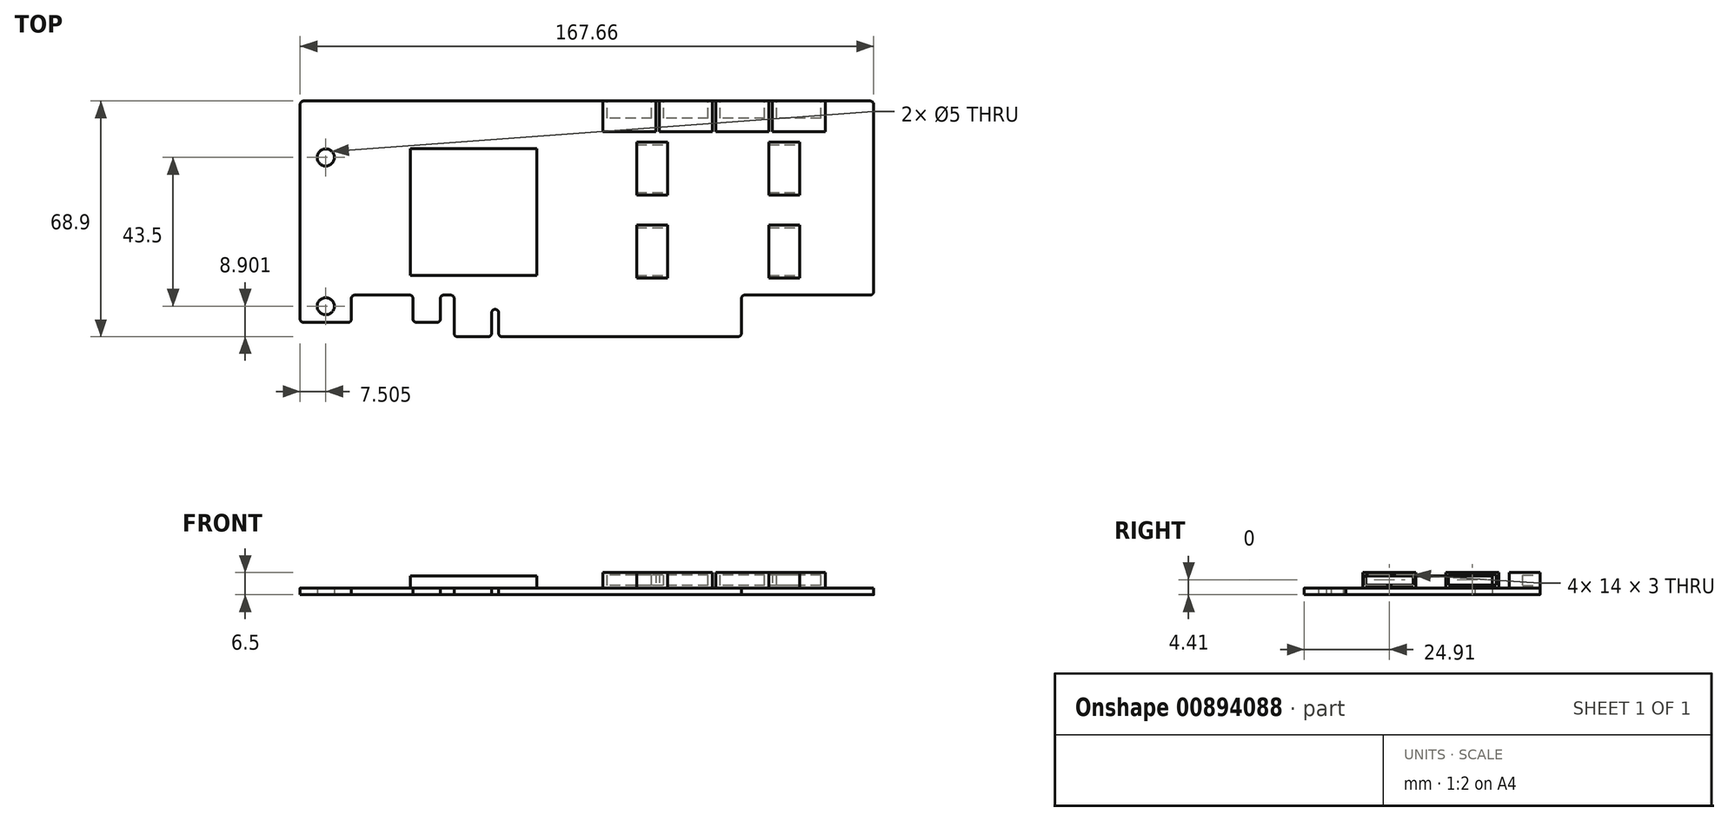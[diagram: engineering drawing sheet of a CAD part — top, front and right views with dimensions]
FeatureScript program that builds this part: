
annotation { "Feature Type Name" : "Feature", "Feature Type Description" : "" }
export const myFeature = defineFeature(function(context is Context, id is Id, definition is map)
    precondition{}
    {
        {
            var Q0;
            Q0=qCreatedBy(makeId("Top.planeOp"),FACE);
            var sketch = newSketch(context, id + "F0", { "sketchPlane" : qUnion([Q0])});
            skLineSegment(sketch, "E0.top", {"start": v(83.83, 32.37) * mm, "end": v(-83.83, 32.37) * mm});
            skLineSegment(sketch, "E0.right", {"start": v(-83.83, -32.37) * mm, "end": v(-83.83, 32.37) * mm});
            skPoint(sketch, "E0.middle", {"position": v(0, 0) * mm});
            skLineSegment(sketch, "E1", {"start": v(-83.83, -32.37) * mm, "end": v(-68.83, -32.37) * mm});
            skLineSegment(sketch, "E2", {"start": v(-68.83, -32.37) * mm, "end": v(-68.83, -24.37) * mm});
            skLineSegment(sketch, "E3", {"start": v(-68.83, -24.37) * mm, "end": v(-50.82, -24.37) * mm});
            skLineSegment(sketch, "E4", {"start": v(-50.82, -24.37) * mm, "end": v(-50.82, -32.37) * mm});
            skLineSegment(sketch, "E5", {"start": v(-50.82, -32.37) * mm, "end": v(-42.83, -32.37) * mm});
            skLineSegment(sketch, "E6", {"start": v(-42.83, -32.37) * mm, "end": v(-42.82, -24.37) * mm});
            skLineSegment(sketch, "E7", {"start": v(-42.82, -24.37) * mm, "end": v(-38.82, -24.37) * mm});
            skLineSegment(sketch, "E8", {"start": v(-38.82, -24.37) * mm, "end": v(-38.82, -36.53) * mm});
            skLineSegment(sketch, "E9", {"start": v(-38.82, -36.53) * mm, "end": v(-27.82, -36.53) * mm});
            skLineSegment(sketch, "E10", {"start": v(-27.82, -36.53) * mm, "end": v(-27.82, -28.53) * mm});
            skLineSegment(sketch, "E11", {"start": v(-27.82, -28.53) * mm, "end": v(-25.82, -28.53) * mm});
            skLineSegment(sketch, "E12", {"start": v(-25.82, -28.53) * mm, "end": v(-25.82, -36.53) * mm});
            skLineSegment(sketch, "E13", {"start": v(-25.82, -36.53) * mm, "end": v(45.18, -36.53) * mm});
            skLineSegment(sketch, "E14", {"start": v(45.18, -36.53) * mm, "end": v(45.18, -24.37) * mm});
            skLineSegment(sketch, "E15", {"start": v(83.83, 32.37) * mm, "end": v(83.83, -24.37) * mm});
            skCircle(sketch, "E16", {"center": v(-76.33, -27.63) * mm, "radius": 2.5 * mm});
            skCircle(sketch, "E17.MirrorC", {"center": v(-76.33, 15.87) * mm, "radius": 2.5 * mm});
            skLineSegment(sketch, "E18", {"start": v(45.18, -24.37) * mm, "end": v(83.82, -24.37) * mm});
            skLineSegment(sketch, "E19", {"start": v(-76.33, 15.87) * mm, "end": v(-76.33, -27.63) * mm, "construction": true});
            skLineSegment(sketch, "E20", {"start": v(-76.33, 15.87) * mm, "end": v(-76.33, 32.37) * mm, "construction": true});
            skLineSegment(sketch, "E21", {"start": v(-83.83, 0) * mm, "end": v(-76.33, 0) * mm, "construction": true});
            skSolve(sketch);
        }
        {
            var Q0;
            Q0=qSketchRegion(id+"F0",true);
            extrude(context, id + "F1", {"entities" : qUnion([Q0]), "depth" : 2 * mm});
        }
        {
            var Q0;
            Q0=makeQuery(id+"F1.opExtrude","CAP_FACE",FACE,{"disambiguationData":[OSD([sQuery(id+"F0.wireOp",EDGE,"E0.top"),sQuery(id+"F0.wireOp",EDGE,"E0.right"),sQuery(id+"F0.wireOp",EDGE,"E1"),sQuery(id+"F0.wireOp",EDGE,"E2"),sQuery(id+"F0.wireOp",EDGE,"E3"),sQuery(id+"F0.wireOp",EDGE,"E4"),sQuery(id+"F0.wireOp",EDGE,"E5"),sQuery(id+"F0.wireOp",EDGE,"E6"),sQuery(id+"F0.wireOp",EDGE,"E7"),sQuery(id+"F0.wireOp",EDGE,"E8"),sQuery(id+"F0.wireOp",EDGE,"E9"),sQuery(id+"F0.wireOp",EDGE,"E10"),sQuery(id+"F0.wireOp",EDGE,"E11"),sQuery(id+"F0.wireOp",EDGE,"E12"),sQuery(id+"F0.wireOp",EDGE,"E13"),sQuery(id+"F0.wireOp",EDGE,"E14"),sQuery(id+"F0.wireOp",EDGE,"E15"),sQuery(id+"F0.wireOp",EDGE,"E16"),sQuery(id+"F0.wireOp",EDGE,"E17.MirrorC"),sQuery(id+"F0.wireOp",EDGE,"E18")])],"isStart":false});
            var sketch = newSketch(context, id + "F2", { "sketchPlane" : qUnion([Q0])});
            skLineSegment(sketch, "E22.bottom", {"start": v(-77.83, 23.37) * mm, "end": v(-62.33, 23.37) * mm});
            skLineSegment(sketch, "E22.top", {"start": v(-77.83, 32.37) * mm, "end": v(-62.33, 32.37) * mm});
            skLineSegment(sketch, "E22.left", {"start": v(-77.83, 23.37) * mm, "end": v(-77.83, 32.37) * mm});
            skLineSegment(sketch, "E22.right", {"start": v(-62.33, 23.37) * mm, "end": v(-62.33, 32.37) * mm});
            skLineSegment(sketch, "E23", {"start": v(-77.83, 32.37) * mm, "end": v(-83.83, 32.37) * mm, "construction": true});
            skLineSegment(sketch, "E24.1.0.0", {"start": v(-61.33, 32.37) * mm, "end": v(-45.83, 32.37) * mm});
            skLineSegment(sketch, "E24.1.0.1", {"start": v(-61.33, 23.37) * mm, "end": v(-61.33, 32.37) * mm});
            skLineSegment(sketch, "E24.1.0.2", {"start": v(-61.33, 23.37) * mm, "end": v(-45.83, 23.37) * mm});
            skLineSegment(sketch, "E24.1.0.3", {"start": v(-45.83, 23.37) * mm, "end": v(-45.83, 32.37) * mm});
            skLineSegment(sketch, "E24.2.0.0", {"start": v(-44.83, 32.37) * mm, "end": v(-29.33, 32.37) * mm});
            skLineSegment(sketch, "E24.2.0.1", {"start": v(-44.83, 23.37) * mm, "end": v(-44.83, 32.37) * mm});
            skLineSegment(sketch, "E24.2.0.2", {"start": v(-44.83, 23.37) * mm, "end": v(-29.33, 23.37) * mm});
            skLineSegment(sketch, "E24.2.0.3", {"start": v(-29.33, 23.37) * mm, "end": v(-29.33, 32.37) * mm});
            skLineSegment(sketch, "E24.direction1", {"start": v(-77.83, 32.37) * mm, "end": v(-61.33, 32.37) * mm, "construction": true});
            skLineSegment(sketch, "E25.0.3.0", {"start": v(-28.33, 32.37) * mm, "end": v(-12.83, 32.37) * mm});
            skLineSegment(sketch, "E25.3.3.0", {"start": v(-28.33, 23.37) * mm, "end": v(-28.33, 32.37) * mm});
            skLineSegment(sketch, "E25.6.3.0", {"start": v(-28.33, 23.37) * mm, "end": v(-12.83, 23.37) * mm});
            skLineSegment(sketch, "E25.9.3.0", {"start": v(-12.83, 23.37) * mm, "end": v(-12.83, 32.37) * mm});
            skLineSegment(sketch, "E25.0.4.0", {"start": v(-11.83, 32.37) * mm, "end": v(3.67, 32.37) * mm});
            skLineSegment(sketch, "E25.3.4.0", {"start": v(-11.83, 23.37) * mm, "end": v(-11.83, 32.37) * mm});
            skLineSegment(sketch, "E25.6.4.0", {"start": v(-11.83, 23.37) * mm, "end": v(3.67, 23.37) * mm});
            skLineSegment(sketch, "E25.9.4.0", {"start": v(3.67, 23.37) * mm, "end": v(3.67, 32.37) * mm});
            skLineSegment(sketch, "E25.0.5.0", {"start": v(4.67, 32.37) * mm, "end": v(20.17, 32.37) * mm});
            skLineSegment(sketch, "E25.3.5.0", {"start": v(4.67, 23.37) * mm, "end": v(4.67, 32.37) * mm});
            skLineSegment(sketch, "E25.6.5.0", {"start": v(4.67, 23.37) * mm, "end": v(20.17, 23.37) * mm});
            skLineSegment(sketch, "E25.9.5.0", {"start": v(20.17, 23.37) * mm, "end": v(20.17, 32.37) * mm});
            skLineSegment(sketch, "E25.0.6.0", {"start": v(21.17, 32.37) * mm, "end": v(36.67, 32.37) * mm});
            skLineSegment(sketch, "E25.3.6.0", {"start": v(21.17, 23.37) * mm, "end": v(21.17, 32.37) * mm});
            skLineSegment(sketch, "E25.6.6.0", {"start": v(21.17, 23.37) * mm, "end": v(36.67, 23.37) * mm});
            skLineSegment(sketch, "E25.9.6.0", {"start": v(36.67, 23.37) * mm, "end": v(36.67, 32.37) * mm});
            skLineSegment(sketch, "E25.0.7.0", {"start": v(37.67, 32.37) * mm, "end": v(53.17, 32.37) * mm});
            skLineSegment(sketch, "E25.3.7.0", {"start": v(37.67, 23.37) * mm, "end": v(37.67, 32.37) * mm});
            skLineSegment(sketch, "E25.6.7.0", {"start": v(37.67, 23.37) * mm, "end": v(53.17, 23.37) * mm});
            skLineSegment(sketch, "E25.9.7.0", {"start": v(53.17, 23.37) * mm, "end": v(53.17, 32.37) * mm});
            skLineSegment(sketch, "E25.0.8.0", {"start": v(54.17, 32.37) * mm, "end": v(69.67, 32.37) * mm});
            skLineSegment(sketch, "E25.3.8.0", {"start": v(54.17, 23.37) * mm, "end": v(54.17, 32.37) * mm});
            skLineSegment(sketch, "E25.6.8.0", {"start": v(54.17, 23.37) * mm, "end": v(69.67, 23.37) * mm});
            skLineSegment(sketch, "E25.9.8.0", {"start": v(69.67, 23.37) * mm, "end": v(69.67, 32.37) * mm});
            skLineSegment(sketch, "E26", {"start": v(53.17, 23.37) * mm, "end": v(53.17, 20.37) * mm, "construction": true});
            skLineSegment(sketch, "E27.bottom", {"start": v(53.17, 20.37) * mm, "end": v(62.17, 20.37) * mm});
            skLineSegment(sketch, "E27.top", {"start": v(53.17, 4.87) * mm, "end": v(62.17, 4.87) * mm});
            skLineSegment(sketch, "E27.left", {"start": v(53.17, 20.37) * mm, "end": v(53.17, 4.87) * mm});
            skLineSegment(sketch, "E27.right", {"start": v(62.17, 20.37) * mm, "end": v(62.17, 4.87) * mm});
            skLineSegment(sketch, "E28.bottom", {"start": v(53.17, -19.37) * mm, "end": v(62.17, -19.37) * mm});
            skLineSegment(sketch, "E28.top", {"start": v(53.17, -3.87) * mm, "end": v(62.17, -3.87) * mm});
            skLineSegment(sketch, "E28.left", {"start": v(53.17, -19.37) * mm, "end": v(53.17, -3.87) * mm});
            skLineSegment(sketch, "E28.right", {"start": v(62.17, -19.37) * mm, "end": v(62.17, -3.87) * mm});
            skLineSegment(sketch, "E29", {"start": v(53.17, 4.87) * mm, "end": v(53.17, -3.87) * mm, "construction": true});
            skLineSegment(sketch, "E30", {"start": v(53.17, -19.37) * mm, "end": v(53.17, -24.37) * mm, "construction": true});
            skLineSegment(sketch, "E31", {"start": v(53.17, 0.5) * mm, "end": v(23.53, 0.5) * mm, "construction": true});
            skLineSegment(sketch, "E32", {"start": v(38.35, 5.58) * mm, "end": v(38.35, -5.04) * mm, "construction": true});
            skPoint(sketch, "E32.startSnap0", {"position": v(38.35, 0.5) * mm});
            skLineSegment(sketch, "E33.MirrorCS", {"start": v(23.53, 20.37) * mm, "end": v(23.53, 4.87) * mm});
            skLineSegment(sketch, "E34.MirrorCS", {"start": v(23.53, 20.37) * mm, "end": v(14.53, 20.37) * mm});
            skLineSegment(sketch, "E35.MirrorCS", {"start": v(14.53, 20.37) * mm, "end": v(14.53, 4.87) * mm});
            skLineSegment(sketch, "E36.MirrorCS", {"start": v(23.53, 4.87) * mm, "end": v(14.53, 4.87) * mm});
            skLineSegment(sketch, "E37.MirrorCS", {"start": v(23.53, -3.87) * mm, "end": v(14.53, -3.87) * mm});
            skLineSegment(sketch, "E38.MirrorCS", {"start": v(23.53, -19.37) * mm, "end": v(23.53, -3.87) * mm});
            skLineSegment(sketch, "E39.MirrorCS", {"start": v(23.53, -19.37) * mm, "end": v(14.53, -19.37) * mm});
            skLineSegment(sketch, "E40.MirrorCS", {"start": v(14.53, -19.37) * mm, "end": v(14.53, -3.87) * mm});
            skLineSegment(sketch, "E41.bottom", {"start": v(-51.64, -18.59) * mm, "end": v(-14.64, -18.59) * mm});
            skLineSegment(sketch, "E41.top", {"start": v(-51.64, 18.41) * mm, "end": v(-14.64, 18.41) * mm});
            skLineSegment(sketch, "E41.left", {"start": v(-51.64, -18.59) * mm, "end": v(-51.64, 18.41) * mm});
            skLineSegment(sketch, "E41.right", {"start": v(-14.64, -18.59) * mm, "end": v(-14.64, 18.41) * mm});
            skSolve(sketch);
        }
        {
            var Q0;
            Q0=makeQuery(id+"F1.opExtrude","SWEPT_EDGE",EDGE,{"disambiguationData":[OSD([sQuery(id+"F0.wireOp",EDGE,"E0.right"),sQuery(id+"F0.wireOp",EDGE,"E1")])]});
            var Q1;
            Q1=makeQuery(id+"F1.opExtrude","SWEPT_EDGE",EDGE,{"disambiguationData":[OSD([sQuery(id+"F0.wireOp",EDGE,"E1"),sQuery(id+"F0.wireOp",EDGE,"E2")])]});
            var Q2;
            Q2=makeQuery(id+"F1.opExtrude","SWEPT_EDGE",EDGE,{"disambiguationData":[OSD([sQuery(id+"F0.wireOp",EDGE,"E2"),sQuery(id+"F0.wireOp",EDGE,"E3")])]});
            var Q3;
            Q3=makeQuery(id+"F1.opExtrude","SWEPT_EDGE",EDGE,{"disambiguationData":[OSD([sQuery(id+"F0.wireOp",EDGE,"E4"),sQuery(id+"F0.wireOp",EDGE,"E5")])]});
            var Q4;
            Q4=makeQuery(id+"F1.opExtrude","SWEPT_EDGE",EDGE,{"disambiguationData":[OSD([sQuery(id+"F0.wireOp",EDGE,"E5"),sQuery(id+"F0.wireOp",EDGE,"E6")])]});
            var Q5;
            Q5=makeQuery(id+"F1.opExtrude","SWEPT_EDGE",EDGE,{"disambiguationData":[OSD([sQuery(id+"F0.wireOp",EDGE,"E6"),sQuery(id+"F0.wireOp",EDGE,"E7")])]});
            var Q6;
            Q6=makeQuery(id+"F1.opExtrude","SWEPT_EDGE",EDGE,{"disambiguationData":[OSD([sQuery(id+"F0.wireOp",EDGE,"E8"),sQuery(id+"F0.wireOp",EDGE,"E9")])]});
            var Q7;
            Q7=makeQuery(id+"F1.opExtrude","SWEPT_EDGE",EDGE,{"disambiguationData":[OSD([sQuery(id+"F0.wireOp",EDGE,"E9"),sQuery(id+"F0.wireOp",EDGE,"E10")])]});
            var Q8;
            Q8=makeQuery(id+"F1.opExtrude","SWEPT_EDGE",EDGE,{"disambiguationData":[OSD([sQuery(id+"F0.wireOp",EDGE,"E10"),sQuery(id+"F0.wireOp",EDGE,"E11")])]});
            var Q9;
            Q9=makeQuery(id+"F1.opExtrude","SWEPT_EDGE",EDGE,{"disambiguationData":[OSD([sQuery(id+"F0.wireOp",EDGE,"E12"),sQuery(id+"F0.wireOp",EDGE,"E13")])]});
            var Q10;
            Q10=makeQuery(id+"F1.opExtrude","SWEPT_EDGE",EDGE,{"disambiguationData":[OSD([sQuery(id+"F0.wireOp",EDGE,"E15"),sQuery(id+"F0.wireOp",EDGE,"E18")])]});
            var Q11;
            Q11=makeQuery(id+"F1.opExtrude","SWEPT_EDGE",EDGE,{"disambiguationData":[OSD([sQuery(id+"F0.wireOp",EDGE,"E14"),sQuery(id+"F0.wireOp",EDGE,"E18")])]});
            var Q12;
            Q12=makeQuery(id+"F1.opExtrude","SWEPT_EDGE",EDGE,{"disambiguationData":[OSD([sQuery(id+"F0.wireOp",EDGE,"E13"),sQuery(id+"F0.wireOp",EDGE,"E14")])]});
            var Q13;
            Q13=makeQuery(id+"F1.opExtrude","SWEPT_EDGE",EDGE,{"disambiguationData":[OSD([sQuery(id+"F0.wireOp",EDGE,"E0.top"),sQuery(id+"F0.wireOp",EDGE,"E15")])]});
            var Q14;
            Q14=makeQuery(id+"F1.opExtrude","SWEPT_EDGE",EDGE,{"disambiguationData":[OSD([sQuery(id+"F0.wireOp",EDGE,"E0.top"),sQuery(id+"F0.wireOp",EDGE,"E0.right")])]});
            var Q15;
            Q15=makeQuery(id+"F1.opExtrude","SWEPT_EDGE",EDGE,{"disambiguationData":[OSD([sQuery(id+"F0.wireOp",EDGE,"E3"),sQuery(id+"F0.wireOp",EDGE,"E4")])]});
            var Q16;
            Q16=makeQuery(id+"F1.opExtrude","SWEPT_EDGE",EDGE,{"disambiguationData":[OSD([sQuery(id+"F0.wireOp",EDGE,"E7"),sQuery(id+"F0.wireOp",EDGE,"E8")])]});
            var Q17;
            Q17=makeQuery(id+"F1.opExtrude","SWEPT_EDGE",EDGE,{"disambiguationData":[OSD([sQuery(id+"F0.wireOp",EDGE,"E11"),sQuery(id+"F0.wireOp",EDGE,"E12")])]});
            fillet(context, id + "F3", {"entities" : qUnion([Q0, Q1, Q2, Q3, Q4, Q5, Q6, Q7, Q8, Q9, Q10, Q11, Q12, Q13, Q14, Q15, Q16, Q17]), "radius" : 1 * mm, "tangentPropagation" : true, "allowEdgeOverflow" : false});
        }
        {
            var Q0;
            Q0=qSketchRegion(id+"F2",true);
            extrude(context, id + "F4", {"entities" : qUnion([Q0]), "operationType" : NewBodyOperationType.REMOVE, "oppositeDirection" : true, "depth" : .5 * mm});
        }
        {
            var Q0;
            Q0=makeQuery(id+"F4.boolean.opBoolean","COPY",FACE,{"derivedFrom":makeQuery(id+"F4.opExtrude","CAP_FACE",FACE,{"disambiguationData":[OSD([sQuery(id+"F2.wireOp",EDGE,"E22.bottom"),sQuery(id+"F2.wireOp",EDGE,"E22.top"),sQuery(id+"F2.wireOp",EDGE,"E22.left"),sQuery(id+"F2.wireOp",EDGE,"E22.right")])],"isStart":false})});
            var Q1;
            Q1=makeQuery(id+"F4.boolean.opBoolean","COPY",FACE,{"derivedFrom":makeQuery(id+"F4.opExtrude","CAP_FACE",FACE,{"disambiguationData":[OSD([sQuery(id+"F2.wireOp",EDGE,"E24.1.0.0"),sQuery(id+"F2.wireOp",EDGE,"E24.1.0.1"),sQuery(id+"F2.wireOp",EDGE,"E24.1.0.2"),sQuery(id+"F2.wireOp",EDGE,"E24.1.0.3")])],"isStart":false})});
            var Q2;
            Q2=makeQuery(id+"F4.boolean.opBoolean","COPY",FACE,{"derivedFrom":makeQuery(id+"F4.opExtrude","CAP_FACE",FACE,{"disambiguationData":[OSD([sQuery(id+"F2.wireOp",EDGE,"E24.2.0.0"),sQuery(id+"F2.wireOp",EDGE,"E24.2.0.1"),sQuery(id+"F2.wireOp",EDGE,"E24.2.0.2"),sQuery(id+"F2.wireOp",EDGE,"E24.2.0.3")])],"isStart":false})});
            var Q3;
            Q3=makeQuery(id+"F4.boolean.opBoolean","COPY",FACE,{"derivedFrom":makeQuery(id+"F4.opExtrude","CAP_FACE",FACE,{"disambiguationData":[OSD([sQuery(id+"F2.wireOp",EDGE,"E25.0.3.0"),sQuery(id+"F2.wireOp",EDGE,"E25.3.3.0"),sQuery(id+"F2.wireOp",EDGE,"E25.6.3.0"),sQuery(id+"F2.wireOp",EDGE,"E25.9.3.0")])],"isStart":false})});
            var Q4;
            Q4=makeQuery(id+"F4.boolean.opBoolean","COPY",FACE,{"derivedFrom":makeQuery(id+"F4.opExtrude","CAP_FACE",FACE,{"disambiguationData":[OSD([sQuery(id+"F2.wireOp",EDGE,"E25.0.4.0"),sQuery(id+"F2.wireOp",EDGE,"E25.3.4.0"),sQuery(id+"F2.wireOp",EDGE,"E25.6.4.0"),sQuery(id+"F2.wireOp",EDGE,"E25.9.4.0")])],"isStart":false})});
            var Q5;
            Q5=makeQuery(id+"F1.opExtrude","CAP_FACE",FACE,{"disambiguationData":[OSD([sQuery(id+"F0.wireOp",EDGE,"E0.top"),sQuery(id+"F0.wireOp",EDGE,"E0.right"),sQuery(id+"F0.wireOp",EDGE,"E1"),sQuery(id+"F0.wireOp",EDGE,"E2"),sQuery(id+"F0.wireOp",EDGE,"E3"),sQuery(id+"F0.wireOp",EDGE,"E4"),sQuery(id+"F0.wireOp",EDGE,"E5"),sQuery(id+"F0.wireOp",EDGE,"E6"),sQuery(id+"F0.wireOp",EDGE,"E7"),sQuery(id+"F0.wireOp",EDGE,"E8"),sQuery(id+"F0.wireOp",EDGE,"E9"),sQuery(id+"F0.wireOp",EDGE,"E10"),sQuery(id+"F0.wireOp",EDGE,"E11"),sQuery(id+"F0.wireOp",EDGE,"E12"),sQuery(id+"F0.wireOp",EDGE,"E13"),sQuery(id+"F0.wireOp",EDGE,"E14"),sQuery(id+"F0.wireOp",EDGE,"E15"),sQuery(id+"F0.wireOp",EDGE,"E16"),sQuery(id+"F0.wireOp",EDGE,"E17.MirrorC"),sQuery(id+"F0.wireOp",EDGE,"E18")])],"isStart":false});
            extrude(context, id + "F5", {"entities" : qUnion([Q0, Q1, Q2, Q3, Q4]), "operationType" : NewBodyOperationType.ADD, "endBound" : BoundingType.UP_TO_SURFACE, "depth" : 25 * mm, "endBoundEntityFace" : qUnion([Q5]), "offsetDistance" : 25 * mm});
        }
        {
            var Q0;
            Q0=makeQuery(id+"F4.boolean.opBoolean","COPY",FACE,{"derivedFrom":makeQuery(id+"F4.opExtrude","CAP_FACE",FACE,{"disambiguationData":[OSD([sQuery(id+"F2.wireOp",EDGE,"E25.0.5.0"),sQuery(id+"F2.wireOp",EDGE,"E25.3.5.0"),sQuery(id+"F2.wireOp",EDGE,"E25.6.5.0"),sQuery(id+"F2.wireOp",EDGE,"E25.9.5.0")])],"isStart":false})});
            var Q1;
            Q1=makeQuery(id+"F4.boolean.opBoolean","COPY",FACE,{"derivedFrom":makeQuery(id+"F4.opExtrude","CAP_FACE",FACE,{"disambiguationData":[OSD([sQuery(id+"F2.wireOp",EDGE,"E25.0.6.0"),sQuery(id+"F2.wireOp",EDGE,"E25.3.6.0"),sQuery(id+"F2.wireOp",EDGE,"E25.6.6.0"),sQuery(id+"F2.wireOp",EDGE,"E25.9.6.0")])],"isStart":false})});
            var Q2;
            Q2=makeQuery(id+"F4.boolean.opBoolean","COPY",FACE,{"derivedFrom":makeQuery(id+"F4.opExtrude","CAP_FACE",FACE,{"disambiguationData":[OSD([sQuery(id+"F2.wireOp",EDGE,"E25.0.7.0"),sQuery(id+"F2.wireOp",EDGE,"E25.3.7.0"),sQuery(id+"F2.wireOp",EDGE,"E25.6.7.0"),sQuery(id+"F2.wireOp",EDGE,"E25.9.7.0")])],"isStart":false})});
            var Q3;
            Q3=makeQuery(id+"F4.boolean.opBoolean","COPY",FACE,{"derivedFrom":makeQuery(id+"F4.opExtrude","CAP_FACE",FACE,{"disambiguationData":[OSD([sQuery(id+"F2.wireOp",EDGE,"E25.0.8.0"),sQuery(id+"F2.wireOp",EDGE,"E25.3.8.0"),sQuery(id+"F2.wireOp",EDGE,"E25.6.8.0"),sQuery(id+"F2.wireOp",EDGE,"E25.9.8.0")])],"isStart":false})});
            var Q4;
            Q4=makeQuery(id+"F4.boolean.opBoolean","COPY",FACE,{"derivedFrom":makeQuery(id+"F4.opExtrude","CAP_FACE",FACE,{"disambiguationData":[OSD([sQuery(id+"F2.wireOp",EDGE,"E33.MirrorCS"),sQuery(id+"F2.wireOp",EDGE,"E34.MirrorCS"),sQuery(id+"F2.wireOp",EDGE,"E35.MirrorCS"),sQuery(id+"F2.wireOp",EDGE,"E36.MirrorCS")])],"isStart":false})});
            var Q5;
            Q5=makeQuery(id+"F4.boolean.opBoolean","COPY",FACE,{"derivedFrom":makeQuery(id+"F4.opExtrude","CAP_FACE",FACE,{"disambiguationData":[OSD([sQuery(id+"F2.wireOp",EDGE,"E27.bottom"),sQuery(id+"F2.wireOp",EDGE,"E27.top"),sQuery(id+"F2.wireOp",EDGE,"E27.left"),sQuery(id+"F2.wireOp",EDGE,"E27.right")])],"isStart":false})});
            var Q6;
            Q6=makeQuery(id+"F4.boolean.opBoolean","COPY",FACE,{"derivedFrom":makeQuery(id+"F4.opExtrude","CAP_FACE",FACE,{"disambiguationData":[OSD([sQuery(id+"F2.wireOp",EDGE,"E37.MirrorCS"),sQuery(id+"F2.wireOp",EDGE,"E38.MirrorCS"),sQuery(id+"F2.wireOp",EDGE,"E39.MirrorCS"),sQuery(id+"F2.wireOp",EDGE,"E40.MirrorCS")])],"isStart":false})});
            var Q7;
            Q7=makeQuery(id+"F4.boolean.opBoolean","COPY",FACE,{"derivedFrom":makeQuery(id+"F4.opExtrude","CAP_FACE",FACE,{"disambiguationData":[OSD([sQuery(id+"F2.wireOp",EDGE,"E28.bottom"),sQuery(id+"F2.wireOp",EDGE,"E28.top"),sQuery(id+"F2.wireOp",EDGE,"E28.left"),sQuery(id+"F2.wireOp",EDGE,"E28.right")])],"isStart":false})});
            extrude(context, id + "F6", {"entities" : qUnion([Q0, Q1, Q2, Q3, Q4, Q5, Q6, Q7]), "operationType" : NewBodyOperationType.ADD, "depth" : 5 * mm, "offsetDistance" : 25 * mm});
        }
        {
            var Q0;
            Q0=makeQuery(id+"F6.opExtrude","SWEPT_FACE",FACE,{"disambiguationData":[OSD([sQuery(id+"F2.wireOp",EDGE,"E38.MirrorCS")])]});
            var sketch = newSketch(context, id + "F7", { "sketchPlane" : qUnion([Q0])});
            skLineSegment(sketch, "E42.bottom", {"start": v(-18.62, 2.91) * mm, "end": v(-4.62, 2.91) * mm});
            skLineSegment(sketch, "E42.top", {"start": v(-18.62, 5.91) * mm, "end": v(-4.62, 5.91) * mm});
            skLineSegment(sketch, "E42.left", {"start": v(-18.62, 2.91) * mm, "end": v(-18.62, 5.91) * mm});
            skLineSegment(sketch, "E42.right", {"start": v(-4.62, 2.91) * mm, "end": v(-4.62, 5.91) * mm});
            skPoint(sketch, "E42.middle", {"position": v(-11.62, 4.41) * mm});
            skPoint(sketch, "E42.middle.positionSnap0", {"position": v(-11.62, 6.5) * mm});
            skPoint(sketch, "E42.centerSnap0", {"position": v(-11.62, 6.5) * mm});
            skPoint(sketch, "E43.0", {"position": v(4.87, 6.5) * mm});
            skLineSegment(sketch, "E44", {"start": v(4.87, 6.5) * mm, "end": v(-3.87, 2) * mm, "construction": true});
            skLineSegment(sketch, "E45", {"start": v(0.5, 5.45) * mm, "end": v(0.5, 4.25) * mm, "construction": true});
            skPoint(sketch, "E45.startSnap0", {"position": v(0.5, 4.25) * mm});
            skLineSegment(sketch, "E46.MirrorCS", {"start": v(5.62, 2.91) * mm, "end": v(5.62, 5.91) * mm});
            skLineSegment(sketch, "E47.MirrorCS", {"start": v(19.62, 5.91) * mm, "end": v(5.62, 5.91) * mm});
            skLineSegment(sketch, "E48.MirrorCS", {"start": v(19.62, 2.91) * mm, "end": v(5.62, 2.91) * mm});
            skLineSegment(sketch, "E49.MirrorCS", {"start": v(19.62, 2.91) * mm, "end": v(19.62, 5.91) * mm});
            skSolve(sketch);
        }
        {
            var Q0;
            Q0 = qSketchRegion(id + "F7", true);
            extrude(context, id + "F8", {"entities" : qUnion([Q0]), "operationType" : NewBodyOperationType.REMOVE, "endBound" : BoundingType.THROUGH_ALL, "oppositeDirection" : true, "depth" : 25 * mm, "offsetDistance" : 25 * mm, "hasSecondDirection" : true, "secondDirectionBound" : SecondDirectionBoundingType.THROUGH_ALL, "secondDirectionOppositeDirection" : false, "secondDirectionDepth" : 25 * mm});
        }
        {
            var Q0;
            Q0=makeQuery(id+"F6.boolean.opBoolean","MERGE",FACE,{"derivedFrom":[makeQuery(id+"F5.boolean.opBoolean","MERGE",FACE,{"derivedFrom":[makeQuery(id+"F1.opExtrude","SWEPT_FACE",FACE,{"disambiguationData":[OSD([sQuery(id+"F0.wireOp",EDGE,"E0.top")])]}),makeQuery(id+"F5.opExtrude","SWEPT_FACE",FACE,{"disambiguationData":[OSD([sQuery(id+"F2.wireOp",EDGE,"E22.top")])]}),makeQuery(id+"F5.opExtrude","SWEPT_FACE",FACE,{"disambiguationData":[OSD([sQuery(id+"F2.wireOp",EDGE,"E24.1.0.0")])]}),makeQuery(id+"F5.opExtrude","SWEPT_FACE",FACE,{"disambiguationData":[OSD([sQuery(id+"F2.wireOp",EDGE,"E24.2.0.0")])]}),makeQuery(id+"F5.opExtrude","SWEPT_FACE",FACE,{"disambiguationData":[OSD([sQuery(id+"F2.wireOp",EDGE,"E25.0.3.0")])]}),makeQuery(id+"F5.opExtrude","SWEPT_FACE",FACE,{"disambiguationData":[OSD([sQuery(id+"F2.wireOp",EDGE,"E25.0.4.0")])]})]}),makeQuery(id+"F6.opExtrude","SWEPT_FACE",FACE,{"disambiguationData":[OSD([sQuery(id+"F2.wireOp",EDGE,"E25.0.5.0")])]}),makeQuery(id+"F6.opExtrude","SWEPT_FACE",FACE,{"disambiguationData":[OSD([sQuery(id+"F2.wireOp",EDGE,"E25.0.6.0")])]}),makeQuery(id+"F6.opExtrude","SWEPT_FACE",FACE,{"disambiguationData":[OSD([sQuery(id+"F2.wireOp",EDGE,"E25.0.7.0")])]}),makeQuery(id+"F6.opExtrude","SWEPT_FACE",FACE,{"disambiguationData":[OSD([sQuery(id+"F2.wireOp",EDGE,"E25.0.8.0")])]})]});
            var sketch = newSketch(context, id + "F9", { "sketchPlane" : qUnion([Q0])});
            skLineSegment(sketch, "E50", {"start": v(-4.67, 6.5) * mm, "end": v(-20.17, 2) * mm, "construction": true});
            skLineSegment(sketch, "E51.bottom", {"start": v(-18.92, 2.75) * mm, "end": v(-5.92, 2.75) * mm});
            skLineSegment(sketch, "E51.top", {"start": v(-18.92, 5.75) * mm, "end": v(-5.92, 5.75) * mm});
            skLineSegment(sketch, "E51.left", {"start": v(-18.92, 2.75) * mm, "end": v(-18.92, 5.75) * mm});
            skLineSegment(sketch, "E51.right", {"start": v(-5.92, 2.75) * mm, "end": v(-5.92, 5.75) * mm});
            skPoint(sketch, "E51.middle", {"position": v(-12.42, 4.25) * mm});
            skLineSegment(sketch, "E52.1.0.0", {"start": v(-35.42, 2.75) * mm, "end": v(-22.42, 2.75) * mm});
            skLineSegment(sketch, "E52.1.0.1", {"start": v(-22.42, 2.75) * mm, "end": v(-22.42, 5.75) * mm});
            skLineSegment(sketch, "E52.1.0.2", {"start": v(-35.42, 5.75) * mm, "end": v(-22.42, 5.75) * mm});
            skLineSegment(sketch, "E52.1.0.3", {"start": v(-35.42, 2.75) * mm, "end": v(-35.42, 5.75) * mm});
            skLineSegment(sketch, "E52.2.0.0", {"start": v(-51.92, 2.75) * mm, "end": v(-38.92, 2.75) * mm});
            skLineSegment(sketch, "E52.2.0.1", {"start": v(-38.92, 2.75) * mm, "end": v(-38.92, 5.75) * mm});
            skLineSegment(sketch, "E52.2.0.2", {"start": v(-51.92, 5.75) * mm, "end": v(-38.92, 5.75) * mm});
            skLineSegment(sketch, "E52.2.0.3", {"start": v(-51.92, 2.75) * mm, "end": v(-51.92, 5.75) * mm});
            skLineSegment(sketch, "E52.3.0.0", {"start": v(-68.42, 2.75) * mm, "end": v(-55.42, 2.75) * mm});
            skLineSegment(sketch, "E52.3.0.1", {"start": v(-55.42, 2.75) * mm, "end": v(-55.42, 5.75) * mm});
            skLineSegment(sketch, "E52.3.0.2", {"start": v(-68.42, 5.75) * mm, "end": v(-55.42, 5.75) * mm});
            skLineSegment(sketch, "E52.3.0.3", {"start": v(-68.42, 2.75) * mm, "end": v(-68.42, 5.75) * mm});
            skLineSegment(sketch, "E52.direction1", {"start": v(-18.92, 2.75) * mm, "end": v(-35.42, 2.75) * mm, "construction": true});
            skSolve(sketch);
        }
        {
            var Q0;
            Q0 = qSketchRegion(id + "F9", true);
            extrude(context, id + "F10", {"entities" : qUnion([Q0]), "operationType" : NewBodyOperationType.REMOVE, "oppositeDirection" : true, "depth" : 5 * mm, "offsetDistance" : 25 * mm});
        }
        {
            var Q0;
            Q0=makeQuery(id+"F4.boolean.opBoolean","COPY",FACE,{"derivedFrom":makeQuery(id+"F4.opExtrude","CAP_FACE",FACE,{"disambiguationData":[OSD([sQuery(id+"F2.wireOp",EDGE,"E41.bottom"),sQuery(id+"F2.wireOp",EDGE,"E41.top"),sQuery(id+"F2.wireOp",EDGE,"E41.left"),sQuery(id+"F2.wireOp",EDGE,"E41.right")])],"isStart":false})});
            extrude(context, id + "F11", {"entities" : qUnion([Q0]), "operationType" : NewBodyOperationType.ADD, "depth" : 4 * mm, "offsetDistance" : 25 * mm});
        }
    });
